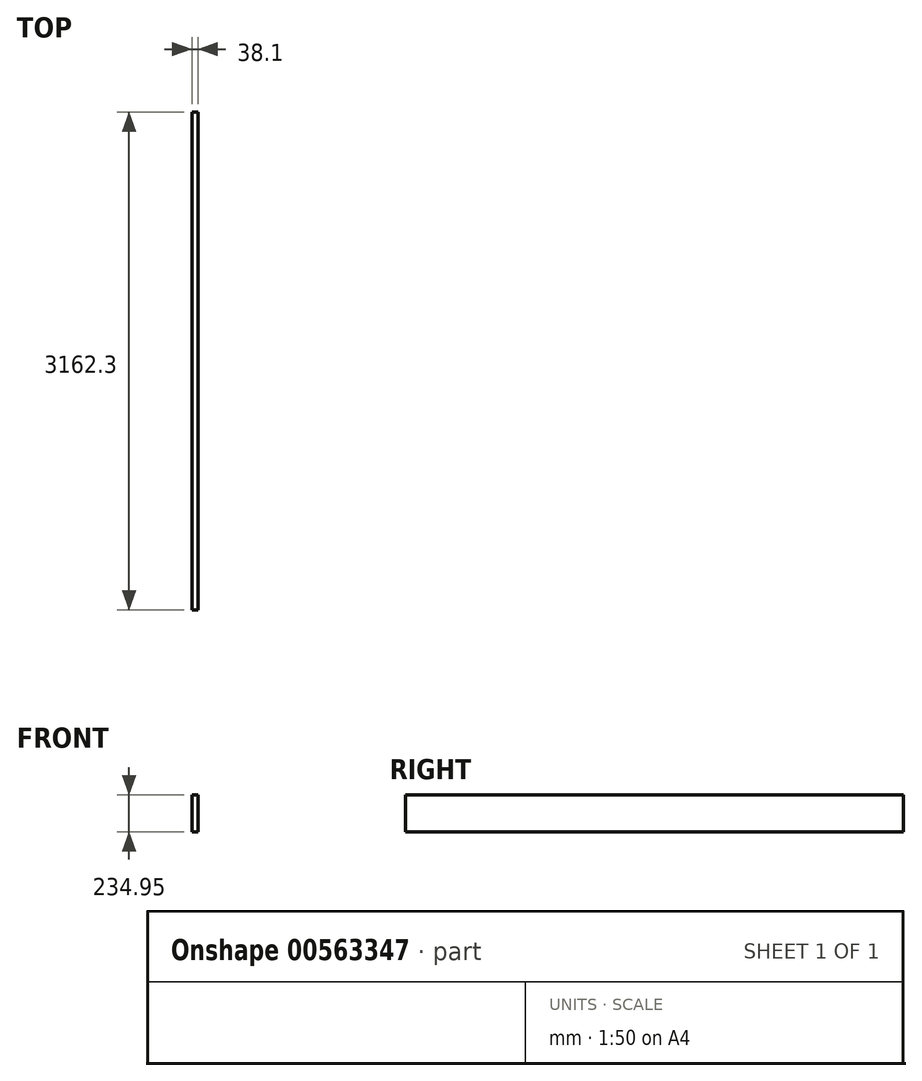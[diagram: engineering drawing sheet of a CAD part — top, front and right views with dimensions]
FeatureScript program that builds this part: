
annotation { "Feature Type Name" : "Feature", "Feature Type Description" : "" }
export const myFeature = defineFeature(function(context is Context, id is Id, definition is map)
    precondition{}
    {
        {
            var Q0;
            Q0=qCreatedBy(makeId("Top.planeOp"),FACE);
            var sketch = newSketch(context, id + "F0", { "sketchPlane" : qUnion([Q0])});
            skLineSegment(sketch, "E0.bottom", {"start": v(19.05, -1581.15) * mm, "end": v(-19.05, -1581.15) * mm});
            skLineSegment(sketch, "E0.top", {"start": v(19.05, 1581.15) * mm, "end": v(-19.05, 1581.15) * mm});
            skLineSegment(sketch, "E0.left", {"start": v(19.05, -1581.15) * mm, "end": v(19.05, 1581.15) * mm});
            skLineSegment(sketch, "E0.right", {"start": v(-19.05, -1581.15) * mm, "end": v(-19.05, 1581.15) * mm});
            skPoint(sketch, "E0.middle", {"position": v(0, 0) * mm});
            skSolve(sketch);
        }
        {
            var Q0;
            Q0 = qSketchRegion(id + "F0", true);
            extrude(context, id + "F1", {"entities" : qUnion([Q0]), "depth" : 234.95 * mm, "offsetDistance" : 25.4 * mm});
        }
    });
